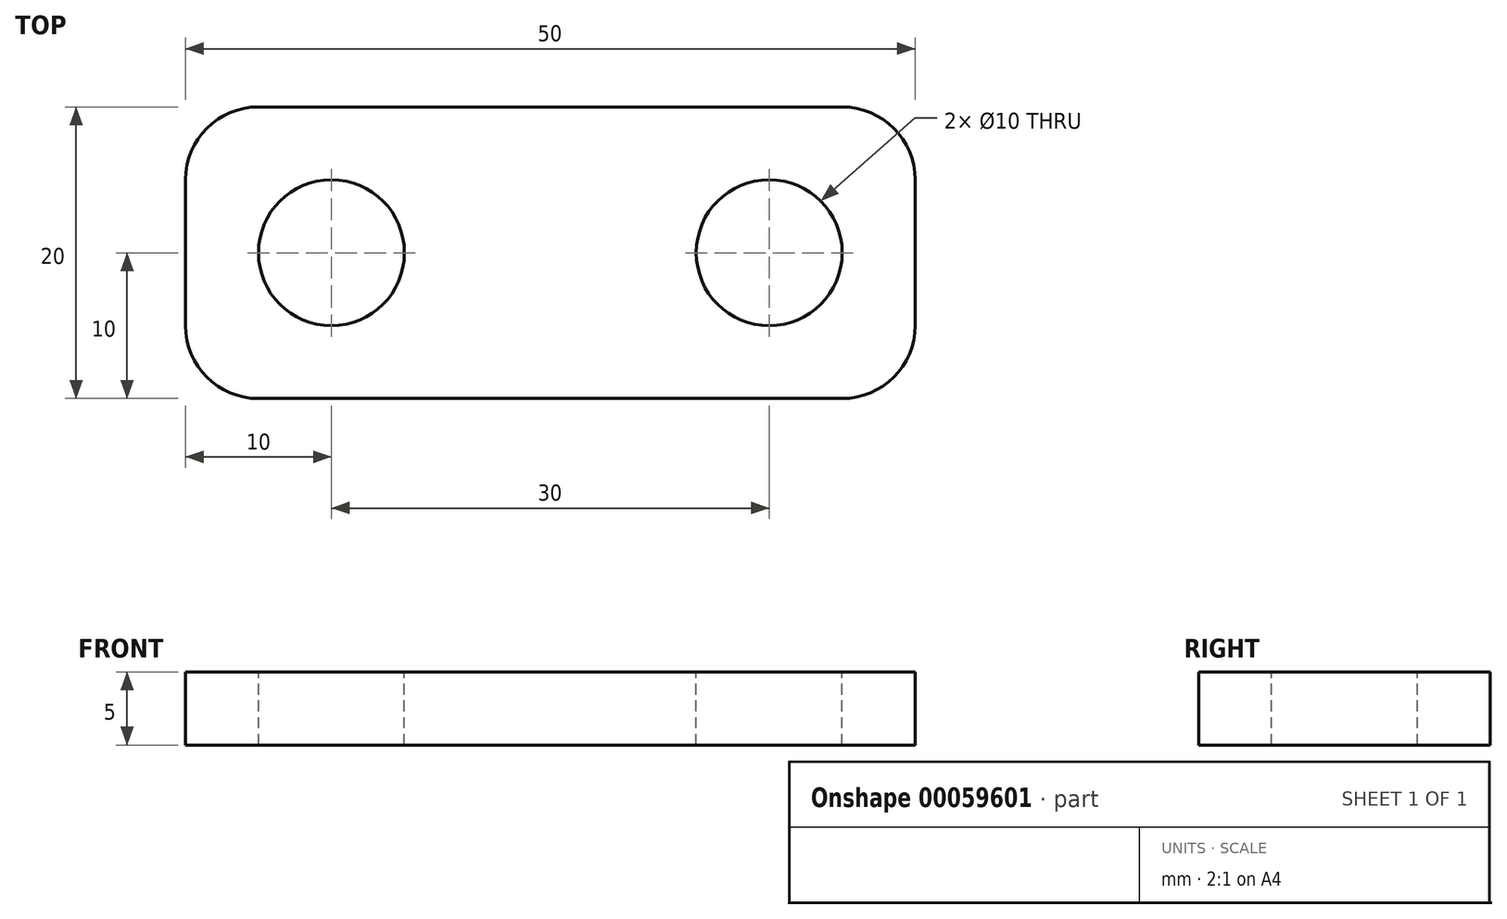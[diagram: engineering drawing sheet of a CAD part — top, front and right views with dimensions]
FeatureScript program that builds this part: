
annotation { "Feature Type Name" : "Feature", "Feature Type Description" : "" }
export const myFeature = defineFeature(function(context is Context, id is Id, definition is map)
    precondition{}
    {
        {
            var Q0;
            Q0=qCreatedBy(makeId("Top.planeOp"),FACE);
            var sketch = newSketch(context, id + "F0", { "sketchPlane" : qUnion([Q0])});
            skLineSegment(sketch, "E0.bottom", {"start": v(-10, 10) * mm, "end": v(40, 10) * mm});
            skLineSegment(sketch, "E0.top", {"start": v(-10, -10) * mm, "end": v(40, -10) * mm});
            skLineSegment(sketch, "E0.left", {"start": v(-10, 10) * mm, "end": v(-10, -10) * mm});
            skLineSegment(sketch, "E0.right", {"start": v(40, 10) * mm, "end": v(40, -10) * mm});
            skSolve(sketch);
        }
        {
            var Q0;
            Q0 = qSketchRegion(id + "F0", true);
            extrude(context, id + "F1", {"entities" : qUnion([Q0]), "depth" : 5 * mm});
        }
        {
            var Q0;
            Q0=makeQuery(id+"F1.opExtrude","CAP_FACE",FACE,{"disambiguationData":[OSD([sQuery(id+"F0.wireOp",EDGE,"E0.bottom"),sQuery(id+"F0.wireOp",EDGE,"E0.top"),sQuery(id+"F0.wireOp",EDGE,"E0.left"),sQuery(id+"F0.wireOp",EDGE,"E0.right")])],"isStart":false});
            var sketch = newSketch(context, id + "F2", { "sketchPlane" : qUnion([Q0])});
            skCircle(sketch, "E1", {"center": v(0, 0) * mm, "radius": 5 * mm});
            skSolve(sketch);
        }
        {
            var Q0;
            Q0 = qSketchRegion(id + "F2", true);
            extrude(context, id + "F3", {"entities" : qUnion([Q0]), "operationType" : NewBodyOperationType.REMOVE, "endBound" : BoundingType.UP_TO_NEXT, "oppositeDirection" : true, "depth" : 25 * mm});
        }
        {
            var Q0;
            Q0=makeQuery(id+"F1.opExtrude","CAP_FACE",FACE,{"disambiguationData":[OSD([sQuery(id+"F0.wireOp",EDGE,"E0.bottom"),sQuery(id+"F0.wireOp",EDGE,"E0.top"),sQuery(id+"F0.wireOp",EDGE,"E0.left"),sQuery(id+"F0.wireOp",EDGE,"E0.right")])],"isStart":false});
            var sketch = newSketch(context, id + "F4", { "sketchPlane" : qUnion([Q0])});
            skCircle(sketch, "E2", {"center": v(30, 0) * mm, "radius": 5 * mm});
            skSolve(sketch);
        }
        {
            var Q0;
            Q0 = qSketchRegion(id + "F4", true);
            extrude(context, id + "F5", {"entities" : qUnion([Q0]), "operationType" : NewBodyOperationType.REMOVE, "endBound" : BoundingType.UP_TO_NEXT, "oppositeDirection" : true, "depth" : 25 * mm});
        }
        {
            var Q0;
            Q0=makeQuery(id+"F1.opExtrude","SWEPT_EDGE",EDGE,{"disambiguationData":[OSD([sQuery(id+"F0.wireOp",EDGE,"E0.bottom"),sQuery(id+"F0.wireOp",EDGE,"E0.left")])]});
            var Q1;
            Q1=makeQuery(id+"F1.opExtrude","SWEPT_EDGE",EDGE,{"disambiguationData":[OSD([sQuery(id+"F0.wireOp",EDGE,"E0.top"),sQuery(id+"F0.wireOp",EDGE,"E0.left")])]});
            var Q2;
            Q2=makeQuery(id+"F1.opExtrude","SWEPT_EDGE",EDGE,{"disambiguationData":[OSD([sQuery(id+"F0.wireOp",EDGE,"E0.bottom"),sQuery(id+"F0.wireOp",EDGE,"E0.right")])]});
            var Q3;
            Q3=makeQuery(id+"F1.opExtrude","SWEPT_EDGE",EDGE,{"disambiguationData":[OSD([sQuery(id+"F0.wireOp",EDGE,"E0.top"),sQuery(id+"F0.wireOp",EDGE,"E0.right")])]});
            fillet(context, id + "F6", {"entities" : qUnion([Q0, Q1, Q2, Q3]), "radius" : 5 * mm, "tangentPropagation" : true, "allowEdgeOverflow" : false});
        }
    });
